# Revit family: Bicorn_Chairs_BIM
name_source: partatom
category: Arredi
units: mm (PartAtom-declared; Revit-internal decimal feet)

## family parameters
Attiva taglio nelle viste = No
Basato su piano di lavoro = No
Condiviso = No
Numero OmniClass = 23.40.20.00
Origine composizione di rendering = Geometria famiglia
Punto di calcolo locali = No
Sempre verticale = Sì
Taglio con vuoti quando caricato = No
Titolo OmniClass = General Furniture and Specialties

## types (2) — shared parameters
AVAILABLE FINISHES = Ebonized black lacquer on Ash (EB) or bleached, white pigment, matte acrylic on Ash (BL). Raw effect lacquer on Oak (RE). Hand rubbed outdoor oil on Iroko (NA). Hand rubbed natural oil on Oak or Walnut (NA), or hand rubbed black oil on Walnut (BO). Base: Tubular stainless steel (SS) or tubular stainless steel with smoke powder coat finish (SP) included in base price, or satin nickel (SN), satin brass (SB), bronze (BZ) or gunmetal (GM) nanoceramic coated tubular stainless steel.
BASE MATERIAL = BASSAM_FELLOWS_OAK_O-NA
BIM BADGE = https://bim.archiproducts.com
COLLECTION = Bicorn
DEPTH = 569 mm
Descrizione = Stackable stainless steel and wood chair with armrests
FEET MATERIAL = BASSAM_FELLOWS_BRONZE_BZ
HEIGHT = 775 mm
PRODUCT SHEET = https://www.archiproducts.com
Produttore = BassamFellows
TECHNICAL SHEET = https://bassamfellows.com
UPHOLSTERY MATERIAL = BASSAM_FELLOWS_ELEGANT_LEATHER_48027_OLIVE
URL = https://bassamfellows.com
WIDTH = 656 mm
zero-valued in all types: Prospetto di default

## per-type parameters (varying)
| type | 59 | 59U | MATERIAL DESCRIPTION | Modello |
| CB-59U | No | Sì | Tubular stainless steel base. Dense foam upholstery over carved wood seat. | Bicorn Chair Upholstered |
| CB-59 | Sì | No | Tubular stainless steel base. Carved wood seat and backrest. | Bicorn Chair |

note: column(s) folded — value = type name in every type: PRODUCT CODE

## geometry (parser evidence)
native form markers: Sweep x2
no freeform markers — native parametric forms only
